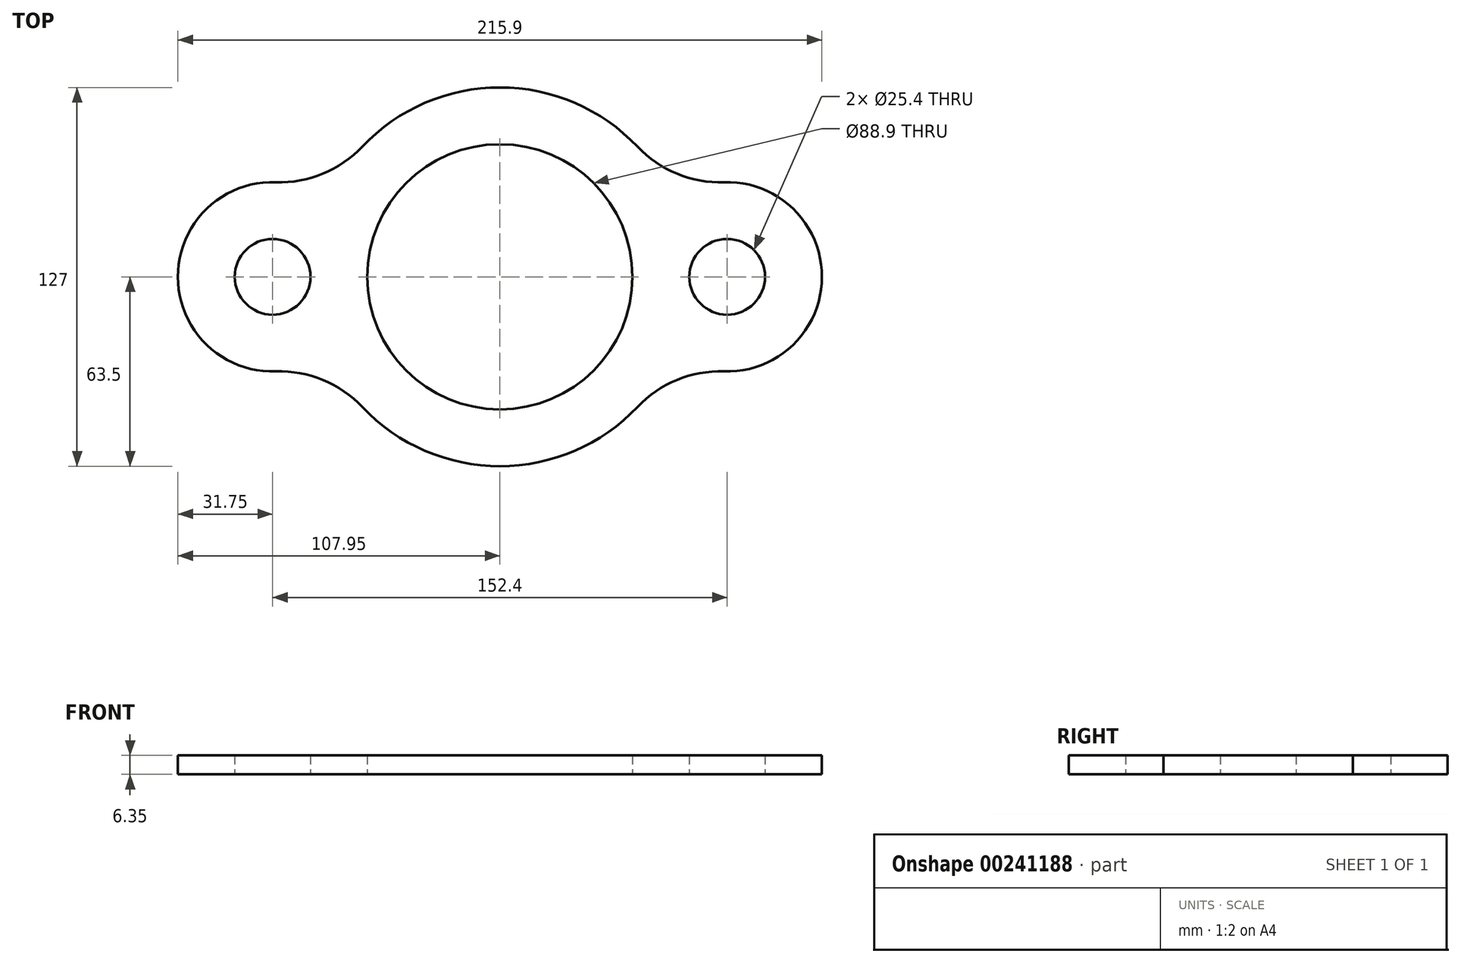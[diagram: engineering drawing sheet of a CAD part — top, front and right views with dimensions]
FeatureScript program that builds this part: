
annotation { "Feature Type Name" : "Feature", "Feature Type Description" : "" }
export const myFeature = defineFeature(function(context is Context, id is Id, definition is map)
    precondition{}
    {
        {
            var Q0;
            Q0=qCreatedBy(makeId("Top.planeOp"),FACE);
            var sketch = newSketch(context, id + "F0", { "sketchPlane" : qUnion([Q0])});
            skCircle(sketch, "E0", {"center": v(0, 0) * mm, "radius": 44.45 * mm});
            skArc(sketch, "E1", {"start": v(-46.14, -43.63) * mm, "mid": v(0, -63.5) * mm, "end": v(46.14, -43.63) * mm});
            skLineSegment(sketch, "E2", {"start": v(0, 0) * mm, "end": v(-76.2, 0) * mm});
            skCircle(sketch, "E3", {"center": v(-76.2, 0) * mm, "radius": 12.7 * mm});
            skArc(sketch, "E4", {"start": v(-75.12, 31.73) * mm, "mid": v(-107.95, 0) * mm, "end": v(-75.12, -31.73) * mm});
            skLineSegment(sketch, "E5", {"start": v(0, 0) * mm, "end": v(44.45, 0) * mm});
            skCircle(sketch, "E6", {"center": v(76.2, 0) * mm, "radius": 12.7 * mm});
            skArc(sketch, "E7", {"start": v(75.12, -31.73) * mm, "mid": v(107.95, 0) * mm, "end": v(75.12, 31.73) * mm});
            skArc(sketch, "E8.trimOffspring", {"start": v(46.14, 43.63) * mm, "mid": v(0, 63.5) * mm, "end": v(-46.14, 43.63) * mm});
            skArc(sketch, "E9.filletArc", {"start": v(-75.12, 31.73) * mm, "mid": v(-59.35, 34.56) * mm, "end": v(-46.14, 43.63) * mm});
            skArc(sketch, "E10.filletArc", {"start": v(46.14, 43.63) * mm, "mid": v(59.35, 34.56) * mm, "end": v(75.12, 31.73) * mm});
            skArc(sketch, "E11.filletArc", {"start": v(75.12, -31.73) * mm, "mid": v(59.35, -34.56) * mm, "end": v(46.14, -43.63) * mm});
            skArc(sketch, "E12.filletArc", {"start": v(-46.14, -43.63) * mm, "mid": v(-59.35, -34.56) * mm, "end": v(-75.12, -31.73) * mm});
            skLineSegment(sketch, "E13", {"start": v(0, 0) * mm, "end": v(76.2, 0) * mm});
            skSolve(sketch);
        }
        {
            var Q0;
            Q0 = qSketchRegion(id + "F0", true);
            extrude(context, id + "F1", {"entities" : qUnion([Q0]), "depth" : 6.35 * mm});
        }
    });
